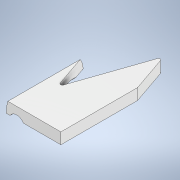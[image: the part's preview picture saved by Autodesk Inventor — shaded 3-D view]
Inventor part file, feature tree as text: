
AUTODESK INVENTOR PART (.ipt)
format: ipt  version: 2021.2 (Build 252289000, 289)  size: 335,360 bytes
history: native  units: in
note: dims shown in document units (in); Inventor stores cm internally (conversion verified against a paired STEP export)
features: sketch x4, extrude x3, hole x1, pattern_linear x1, plane x1, mirror x1
ambient origin geometry x8: Origin, YZ Plane, XZ Plane, XY Plane, X Axis, Y Axis, Z Axis, Center Point
bodies: Solid1 (feature_tree)
feature tree (11):
  extrude  "Extrusion1"  Depth=4.0in
  hole  "Hole2"  [1 undecoded]
  pattern_linear  "Rectangular Pattern1"  Spacing1=0.45in  [1 undecoded]
  extrude  "ExtrusionForText"  Depth=0.125in
  plane  "Work Plane1"
  mirror  "MirrorHoles"
  extrude  "Extrusion3"  Depth=0.125in TaperAngle=0.0deg
  sketch  "Sketch2"  dims[d0=6.0in d1=4.0in]
  sketch  "Sketch3"  dims[d2=0.8189in d4=1.135in]
  sketch  "SketchForText"  dims[d5=0.765in]
  sketch  "SketchForSplittingPart"  dims[d6=11.25in d7=0.0in d8=0.45in d16=0.13in d17=0.6in d18=0.563in d19=0.155in d20=0.5635in d21=0.625in d22=0.8108in d23=3.1496in d25=0.25in d26=0.05in d27=0.0in d30=0.125in d31=0.125in d32=-2.0in d33=0.0in d34=0.0in]
note: 2 required parameter values undecoded (feature->parameter linkage not recoverable at this tier; creation-order binding heuristic only, values carry confidence <= 0.55)
